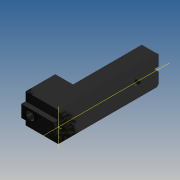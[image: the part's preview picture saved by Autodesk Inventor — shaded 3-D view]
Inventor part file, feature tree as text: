
AUTODESK INVENTOR PART (.ipt)
format: ipt  version: 2017 (Build 210142000, 142)  size: 248,832 bytes
history: native  units: mm
features: sketch x6, extrude x3, hole x3, fillet x2, mirror x1
ambient origin geometry x8: Origin, YZ Plane, XZ Plane, XY Plane, X Axis, Y Axis, Z Axis, Center Point
bodies: Solid1 (feature_tree)
feature tree (15):
  extrude  "Extrusion1"  Depth=10.0mm
  extrude  "Extrusion2"  Depth=20.0mm
  hole  "Hole2"  [1 undecoded]
  hole  "Perçage3"  [1 undecoded]
  fillet  "Congé2"  Radius=16.0mm
  fillet  "Congé3"  Radius=54.0mm
  hole  "Perçage4"  [1 undecoded]
  extrude  "Extrusion3"  Depth=2.0mm
  mirror  "Symétrie1"
  sketch  "Sketch1"  dims[d0=68.0mm d1=10.0mm]
  sketch  "Sketch2"  dims[d2=22.0mm d3=20.0mm]
  sketch  "Sketch4"  dims[d4=20.0mm d5=0.0mm d6=8.2mm d7=3.0mm d8=0.0mm d18=16.0mm d19=5.3mm d20=6.0mm d21=10.0mm d22=6.0mm d23=90.0deg d24=8.0mm d25=20.594885mm d28=54.0mm d29=5.0mm d30=6.0mm d31=4.0mm d32=2.0mm d33=90.0deg d34=8.0mm d35=20.594885mm d36=2.0mm d37=2.0mm d38=54.0mm d39=10.5mm d40=6.0mm d41=4.0mm d42=2.0mm d43=90.0deg d44=6.0mm d45=0.0mm d50=54.0mm d51=3.0mm d52=10.0mm d53=16.803301mm d54=8.939608mm d55=93.232253mm d56=10.0mm d57=0.0mm]
  sketch  "Esquisse5"
  sketch  "Esquisse6"
  sketch  "Esquisse8"
note: 3 required parameter values undecoded (feature->parameter linkage not recoverable at this tier; creation-order binding heuristic only, values carry confidence <= 0.55)
